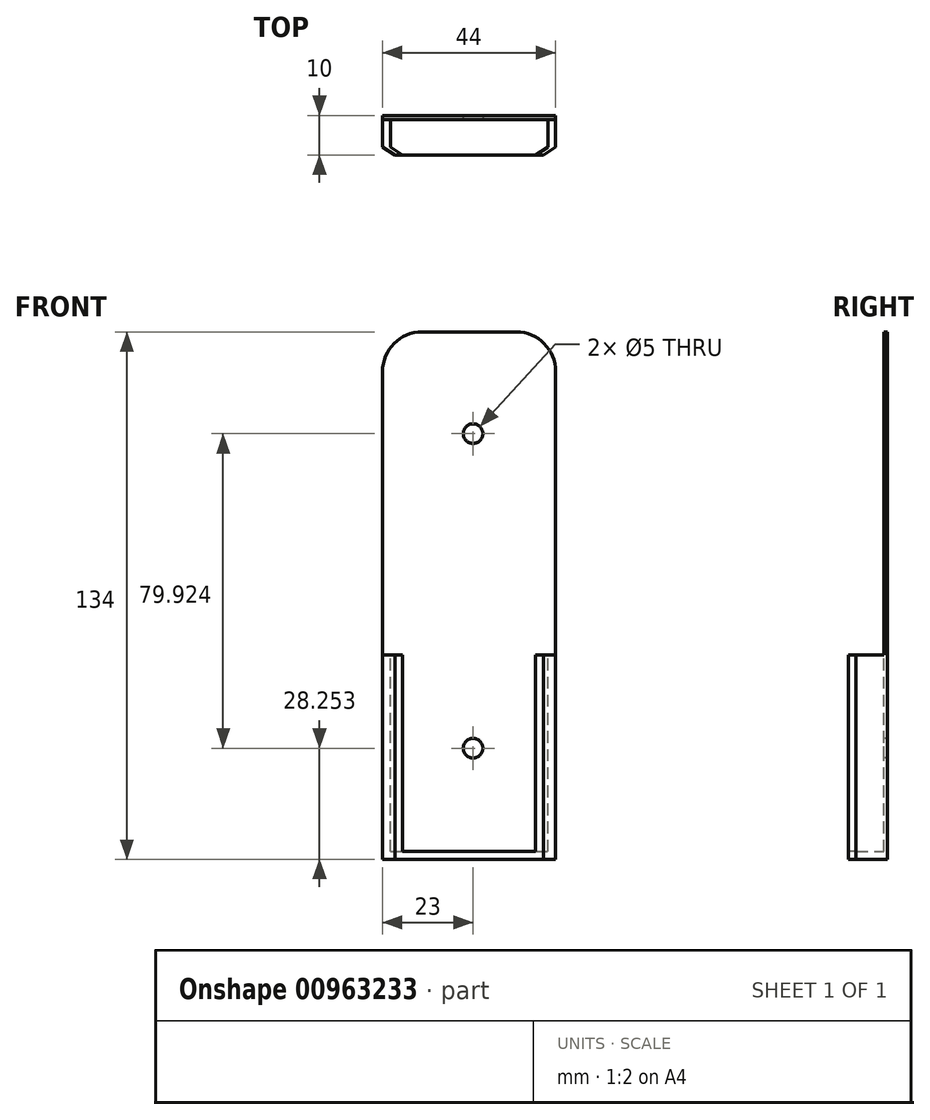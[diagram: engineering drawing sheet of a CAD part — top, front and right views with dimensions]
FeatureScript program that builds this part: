
annotation { "Feature Type Name" : "Feature", "Feature Type Description" : "" }
export const myFeature = defineFeature(function(context is Context, id is Id, definition is map)
    precondition{}
    {
        {
            var Q0;
            Q0=qCreatedBy(makeId("Front.planeOp"),FACE);
            var sketch = newSketch(context, id + "F0", { "sketchPlane" : qUnion([Q0])});
            skLineSegment(sketch, "E0.bottom", {"start": v(0, 0) * mm, "end": v(40, 0) * mm});
            skLineSegment(sketch, "E0.top", {"start": v(0, 130) * mm, "end": v(40, 130) * mm});
            skLineSegment(sketch, "E0.left", {"start": v(0, 0) * mm, "end": v(0, 130) * mm});
            skLineSegment(sketch, "E0.right", {"start": v(40, 0) * mm, "end": v(40, 130) * mm});
            skLineSegment(sketch, "E1.0", {"start": v(-2, -2) * mm, "end": v(-2, 132) * mm});
            skLineSegment(sketch, "E1.1", {"start": v(-2, -2) * mm, "end": v(42, -2) * mm});
            skLineSegment(sketch, "E1.2", {"start": v(42, -2) * mm, "end": v(42, 132) * mm});
            skLineSegment(sketch, "E1.3", {"start": v(-2, 132) * mm, "end": v(42, 132) * mm});
            skSolve(sketch);
        }
        {
            var Q0;
            Q0 = qSketchRegion(id + "F0", true);
            var Q1;
            Q1=makeQuery(id+"F0.imprint","IMPRINT",FACE,{"disambiguationData":[TD([[makeQuery(id+"F0.imprint","IMPRINT",EDGE,{"derivedFrom":sQuery(id+"F0.wireOp",EDGE,"E0.bottom")}),1.0]])]});
            extrude(context, id + "F1", {"entities" : qUnion([Q0, Q1]), "depth" : 1 * mm, "offsetDistance" : 25 * mm});
        }
        {
            var Q0;
            Q0=makeQuery(id+"F1.opExtrude","CAP_FACE",FACE,{"disambiguationData":[OSD([sQuery(id+"F0.wireOp",EDGE,"E1.0"),sQuery(id+"F0.wireOp",EDGE,"E1.1"),sQuery(id+"F0.wireOp",EDGE,"E1.2"),sQuery(id+"F0.wireOp",EDGE,"E1.3")])],"isStart":false});
            var sketch = newSketch(context, id + "F2", { "sketchPlane" : qUnion([Q0])});
            skLineSegment(sketch, "E2.bottom", {"start": v(-2, -2) * mm, "end": v(42, -2) * mm});
            skLineSegment(sketch, "E2.top", {"start": v(-2, 132) * mm, "end": v(42, 132) * mm});
            skLineSegment(sketch, "E2.left", {"start": v(-2, -2) * mm, "end": v(-2, 132) * mm});
            skLineSegment(sketch, "E2.right", {"start": v(42, -2) * mm, "end": v(42, 132) * mm});
            skLineSegment(sketch, "E3.0", {"start": v(0, 130) * mm, "end": v(40, 130) * mm});
            skLineSegment(sketch, "E3.1", {"start": v(0, 0) * mm, "end": v(0, 130) * mm});
            skLineSegment(sketch, "E3.2", {"start": v(0, 0) * mm, "end": v(40, 0) * mm});
            skLineSegment(sketch, "E3.3", {"start": v(40, 0) * mm, "end": v(40, 130) * mm});
            skLineSegment(sketch, "E4", {"start": v(-2, 40) * mm, "end": v(0, 40) * mm});
            skLineSegment(sketch, "E5.trimOffspring", {"start": v(40, 40) * mm, "end": v(42, 40) * mm});
            skSolve(sketch);
        }
        {
            var Q0;
            {var subQ1=sQuery(id+"F2.wireOp",EDGE,"E2.bottom");Q0=makeQuery(id+"F2.imprint","IMPRINT",FACE,{"disambiguationData":[TD([[makeQuery(id+"F2.imprint","IMPRINT",EDGE,{"derivedFrom":subQ1}),1.0]])]});}
            extrude(context, id + "F3", {"entities" : qUnion([Q0]), "operationType" : NewBodyOperationType.ADD, "depth" : 7 * mm, "offsetDistance" : 25 * mm});
        }
        {
            var Q0;
            Q0=makeQuery(id+"F3.boolean.opBoolean","MERGE",FACE,{"derivedFrom":[makeQuery(id+"F1.opExtrude","SWEPT_FACE",FACE,{"disambiguationData":[OSD([sQuery(id+"F0.wireOp",EDGE,"E1.1")])]}),makeQuery(id+"F3.opExtrude","SWEPT_FACE",FACE,{"disambiguationData":[OSD([sQuery(id+"F2.wireOp",EDGE,"E2.bottom")])]})]});
            var sketch = newSketch(context, id + "F4", { "sketchPlane" : qUnion([Q0])});
            skLineSegment(sketch, "E6", {"start": v(-2, 8) * mm, "end": v(1.12, 10) * mm});
            skLineSegment(sketch, "E7", {"start": v(20, 17.2) * mm, "end": v(20, -8.59) * mm, "construction": true});
            skPoint(sketch, "E7.startSnap0", {"position": v(20, 8) * mm});
            skLineSegment(sketch, "E8", {"start": v(1.12, 10) * mm, "end": v(3.12, 10) * mm});
            skLineSegment(sketch, "E9", {"start": v(0, 8) * mm, "end": v(3.12, 10) * mm});
            skLineSegment(sketch, "E10", {"start": v(0, 8) * mm, "end": v(-2, 8) * mm});
            skLineSegment(sketch, "E11.MirrorCS", {"start": v(40, 8) * mm, "end": v(36.88, 10) * mm});
            skLineSegment(sketch, "E12.MirrorCS", {"start": v(38.88, 10) * mm, "end": v(36.88, 10) * mm});
            skLineSegment(sketch, "E13.MirrorCS", {"start": v(40, 8) * mm, "end": v(42, 8) * mm});
            skLineSegment(sketch, "E14.MirrorCS", {"start": v(42, 8) * mm, "end": v(38.88, 10) * mm});
            skSolve(sketch);
        }
        {
            var Q0;
            Q0 = qSketchRegion(id + "F4", true);
            extrude(context, id + "F5", {"entities" : qUnion([Q0]), "operationType" : NewBodyOperationType.ADD, "oppositeDirection" : true, "depth" : 42 * mm, "offsetDistance" : 25 * mm});
        }
        {
            var Q0;
            Q0=makeQuery(id+"F5.boolean.opBoolean","MERGE",FACE,{"derivedFrom":[makeQuery(id+"F3.boolean.opBoolean","MERGE",FACE,{"derivedFrom":[makeQuery(id+"F1.opExtrude","SWEPT_FACE",FACE,{"disambiguationData":[OSD([sQuery(id+"F0.wireOp",EDGE,"E1.1")])]}),makeQuery(id+"F3.opExtrude","SWEPT_FACE",FACE,{"disambiguationData":[OSD([sQuery(id+"F2.wireOp",EDGE,"E2.bottom")])]})]}),makeQuery(id+"F5.opExtrude","CAP_FACE",FACE,{"disambiguationData":[OSD([sQuery(id+"F4.wireOp",EDGE,"E6"),sQuery(id+"F4.wireOp",EDGE,"E8"),sQuery(id+"F4.wireOp",EDGE,"E9"),sQuery(id+"F4.wireOp",EDGE,"E10")])],"isStart":true}),makeQuery(id+"F5.opExtrude","CAP_FACE",FACE,{"disambiguationData":[OSD([sQuery(id+"F4.wireOp",EDGE,"E11.MirrorCS"),sQuery(id+"F4.wireOp",EDGE,"E12.MirrorCS"),sQuery(id+"F4.wireOp",EDGE,"E13.MirrorCS"),sQuery(id+"F4.wireOp",EDGE,"E14.MirrorCS")])],"isStart":true})]});
            var sketch = newSketch(context, id + "F6", { "sketchPlane" : qUnion([Q0])});
            skLineSegment(sketch, "E15", {"start": v(3.12, 10) * mm, "end": v(36.88, 10) * mm});
            skLineSegment(sketch, "E16", {"start": v(36.88, 10) * mm, "end": v(40, 8) * mm});
            skLineSegment(sketch, "E17", {"start": v(40, 8) * mm, "end": v(0, 8) * mm});
            skLineSegment(sketch, "E18", {"start": v(0, 8) * mm, "end": v(3.12, 10) * mm});
            skSolve(sketch);
        }
        {
            var Q0;
            Q0 = qSketchRegion(id + "F6", true);
            extrude(context, id + "F7", {"entities" : qUnion([Q0]), "operationType" : NewBodyOperationType.ADD, "oppositeDirection" : true, "depth" : 2 * mm, "offsetDistance" : 25 * mm});
        }
        {
            var Q0;
            Q0=makeQuery(id+"F5.boolean.opBoolean","MERGE",FACE,{"derivedFrom":[makeQuery(id+"F3.opExtrude","SWEPT_FACE",FACE,{"disambiguationData":[OSD([sQuery(id+"F2.wireOp",EDGE,"E4")])]}),makeQuery(id+"F5.opExtrude","CAP_FACE",FACE,{"disambiguationData":[OSD([sQuery(id+"F4.wireOp",EDGE,"E6"),sQuery(id+"F4.wireOp",EDGE,"E8"),sQuery(id+"F4.wireOp",EDGE,"E9"),sQuery(id+"F4.wireOp",EDGE,"E10")])],"isStart":false})]});
            var sketch = newSketch(context, id + "F8", { "sketchPlane" : qUnion([Q0])});
            skLineSegment(sketch, "E19", {"start": v(-2, -1) * mm, "end": v(0, -1) * mm});
            skLineSegment(sketch, "E20", {"start": v(0, -1) * mm, "end": v(0, -8) * mm});
            skLineSegment(sketch, "E21", {"start": v(0, -8) * mm, "end": v(3.12, -10) * mm});
            skLineSegment(sketch, "E22", {"start": v(3.12, -10) * mm, "end": v(1.12, -10) * mm});
            skLineSegment(sketch, "E23", {"start": v(1.12, -10) * mm, "end": v(-2, -8) * mm});
            skLineSegment(sketch, "E24", {"start": v(-2, -8) * mm, "end": v(-2, -1) * mm});
            skSolve(sketch);
        }
        {
            var Q0;
            Q0 = qSketchRegion(id + "F8", true);
            extrude(context, id + "F9", {"entities" : qUnion([Q0]), "operationType" : NewBodyOperationType.ADD, "depth" : 10 * mm, "offsetDistance" : 25 * mm});
        }
        {
            var Q0;
            Q0=makeQuery(id+"F5.boolean.opBoolean","MERGE",FACE,{"derivedFrom":[makeQuery(id+"F3.opExtrude","SWEPT_FACE",FACE,{"disambiguationData":[OSD([sQuery(id+"F2.wireOp",EDGE,"E5.trimOffspring")])]}),makeQuery(id+"F5.opExtrude","CAP_FACE",FACE,{"disambiguationData":[OSD([sQuery(id+"F4.wireOp",EDGE,"E11.MirrorCS"),sQuery(id+"F4.wireOp",EDGE,"E12.MirrorCS"),sQuery(id+"F4.wireOp",EDGE,"E13.MirrorCS"),sQuery(id+"F4.wireOp",EDGE,"E14.MirrorCS")])],"isStart":false})]});
            var sketch = newSketch(context, id + "F10", { "sketchPlane" : qUnion([Q0])});
            skLineSegment(sketch, "E25", {"start": v(36.88, -10) * mm, "end": v(38.88, -10) * mm});
            skLineSegment(sketch, "E26", {"start": v(38.88, -10) * mm, "end": v(42, -8) * mm});
            skLineSegment(sketch, "E27", {"start": v(42, -8) * mm, "end": v(42, -1) * mm});
            skLineSegment(sketch, "E28", {"start": v(42, -1) * mm, "end": v(40, -1) * mm});
            skLineSegment(sketch, "E29", {"start": v(40, -1) * mm, "end": v(40, -8) * mm});
            skLineSegment(sketch, "E30", {"start": v(40, -8) * mm, "end": v(36.88, -10) * mm});
            skSolve(sketch);
        }
        {
            var Q0;
            Q0 = qSketchRegion(id + "F10", true);
            extrude(context, id + "F11", {"entities" : qUnion([Q0]), "operationType" : NewBodyOperationType.ADD, "depth" : 10 * mm, "offsetDistance" : 25 * mm});
        }
        {
            var Q0;
            Q0=makeQuery(id+"F1.opExtrude","CAP_FACE",FACE,{"disambiguationData":[OSD([sQuery(id+"F0.wireOp",EDGE,"E1.0"),sQuery(id+"F0.wireOp",EDGE,"E1.1"),sQuery(id+"F0.wireOp",EDGE,"E1.2"),sQuery(id+"F0.wireOp",EDGE,"E1.3")])],"isStart":false});
            var sketch = newSketch(context, id + "F12", { "sketchPlane" : qUnion([Q0])});
            skCircle(sketch, "E31", {"center": v(21, 26.25) * mm, "radius": 2.5 * mm});
            skCircle(sketch, "E32", {"center": v(21, 106.18) * mm, "radius": 2.5 * mm});
            skSolve(sketch);
        }
        {
            var Q0;
            Q0 = qSketchRegion(id + "F12", true);
            extrude(context, id + "F13", {"entities" : qUnion([Q0]), "operationType" : NewBodyOperationType.REMOVE, "oppositeDirection" : true, "depth" : 25 * mm, "offsetDistance" : 25 * mm});
        }
        {
            var Q0;
            Q0=makeQuery(id+"F1.opExtrude","CAP_FACE",FACE,{"disambiguationData":[OSD([sQuery(id+"F0.wireOp",EDGE,"E1.0"),sQuery(id+"F0.wireOp",EDGE,"E1.1"),sQuery(id+"F0.wireOp",EDGE,"E1.2"),sQuery(id+"F0.wireOp",EDGE,"E1.3")])],"isStart":false});
            var sketch = newSketch(context, id + "F14", { "sketchPlane" : qUnion([Q0])});
            skLineSegment(sketch, "E33", {"start": v(-2, 102.7) * mm, "end": v(-2, 122) * mm});
            skLineSegment(sketch, "E34", {"start": v(8, 132) * mm, "end": v(32, 132) * mm});
            skLineSegment(sketch, "E35", {"start": v(42, 122) * mm, "end": v(42, 102.7) * mm});
            skLineSegment(sketch, "E36", {"start": v(42, 102.7) * mm, "end": v(116.9, 102.7) * mm});
            skLineSegment(sketch, "E37", {"start": v(116.9, 102.7) * mm, "end": v(116.9, 166.93) * mm});
            skLineSegment(sketch, "E38", {"start": v(116.9, 166.93) * mm, "end": v(-46.18, 166.93) * mm});
            skLineSegment(sketch, "E39", {"start": v(-46.18, 166.93) * mm, "end": v(-46.18, 102.7) * mm});
            skLineSegment(sketch, "E40", {"start": v(-46.18, 102.7) * mm, "end": v(-2, 102.7) * mm});
            skPoint(sketch, "E41.visualSharp", {"position": v(-2, 132) * mm});
            skArc(sketch, "E41.filletArc", {"start": v(8, 132) * mm, "mid": v(0.93, 129.07) * mm, "end": v(-2, 122) * mm});
            skPoint(sketch, "E42.visualSharp", {"position": v(42, 132) * mm});
            skArc(sketch, "E42.filletArc", {"start": v(42, 122) * mm, "mid": v(39.07, 129.07) * mm, "end": v(32, 132) * mm});
            skSolve(sketch);
        }
        {
            var Q0;
            Q0 = qSketchRegion(id + "F14", true);
            extrude(context, id + "F15", {"entities" : qUnion([Q0]), "operationType" : NewBodyOperationType.REMOVE, "oppositeDirection" : true, "depth" : 25 * mm, "offsetDistance" : 25 * mm});
        }
    });
